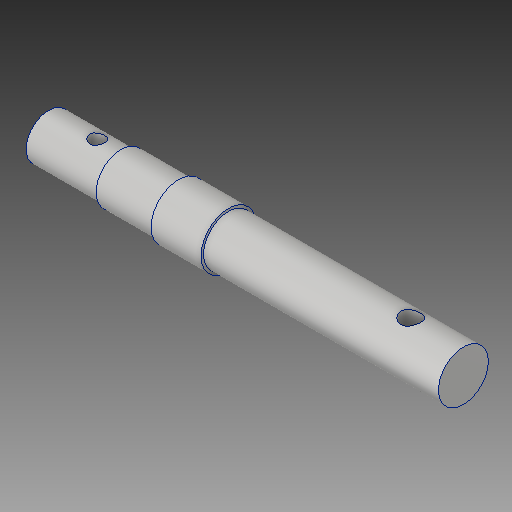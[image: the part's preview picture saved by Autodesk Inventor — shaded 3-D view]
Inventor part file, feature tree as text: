
AUTODESK INVENTOR PART (.ipt)
format: ipt  version: 2018 (Build 220112000, 112)  size: 135,680 bytes
history: native  units: mm
features: sketch x3, other x2, revolve x1, extrude x1, hole x1
ambient origin geometry x8: Origin, YZ Plane, XZ Plane, XY Plane, X Axis, Y Axis, Z Axis, Center Point
bodies: Body1 (feature_tree)
feature tree (8):
  other  "ソリッド1"
  revolve  "回転1"
  extrude  "押し出し2"  Depth=11.0mm
  other  "作業平面1"
  hole  "穴1"  [1 undecoded]
  sketch  "スケッチ1"
  sketch  "スケッチ2"
  sketch  "スケッチ3"
note: 1 required parameter value undecoded (feature->parameter linkage not recoverable at this tier; creation-order binding heuristic only, values carry confidence <= 0.55)
